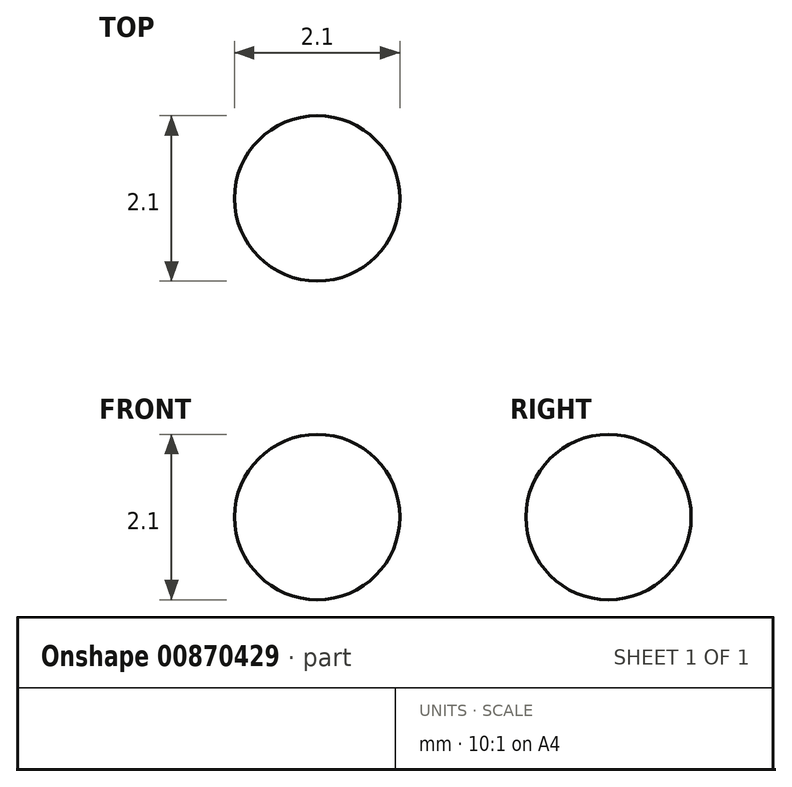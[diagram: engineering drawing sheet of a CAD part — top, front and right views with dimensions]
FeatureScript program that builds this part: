
annotation { "Feature Type Name" : "Feature", "Feature Type Description" : "" }
export const myFeature = defineFeature(function(context is Context, id is Id, definition is map)
    precondition{}
    {
        {
            var Q0;
            Q0=qCreatedBy(makeId("Front.planeOp"),FACE);
            var sketch = newSketch(context, id + "F0", { "sketchPlane" : qUnion([Q0])});
            skArc(sketch, "E0", {"start": v(0, 11.6) * mm, "mid": v(-1.05, 10.54) * mm, "end": v(0, 9.5) * mm});
            skLineSegment(sketch, "E1", {"start": v(0, 11.6) * mm, "end": v(0, 9.5) * mm});
            skSolve(sketch);
        }
        {
            var Q0;
            Q0 = qSketchRegion(id + "F0", true);
            var Q1;
            Q1=sQuery(id+"F0.wireOp",EDGE,"E1");
            revolve(context, id + "F1", {"surfaceOperationType" : NewSurfaceOperationType.NEW, "entities" : qUnion([Q0]), "axis" : qUnion([Q1]), "revolveType" : RevolveType.FULL});
        }
    });
